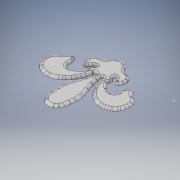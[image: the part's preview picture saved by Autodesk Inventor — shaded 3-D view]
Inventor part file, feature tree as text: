
AUTODESK INVENTOR PART (.ipt)
format: ipt  version: 2019 (Build 230136000, 136)  size: 981,504 bytes
history: native  units: mm
features: fillet x12, sketch x3, extrude x2
ambient origin geometry x8: Origin, YZ Plane, XZ Plane, XY Plane, X Axis, Y Axis, Z Axis, Center Point
bodies: Solid1 (feature_tree)
feature tree (17):
  extrude  "Extrusion1"  Depth=800.0mm
  fillet  "Fillet1"  Radius=300.0mm
  fillet  "Fillet2"  Radius=400.0mm
  fillet  "Fillet3"  Radius=200.0mm
  fillet  "Fillet4"  Radius=600.0mm
  fillet  "Fillet5"  Radius=1200.0mm
  fillet  "Fillet6"  Radius=2000.0mm
  fillet  "Fillet7"  Radius=100.0mm
  fillet  "Fillet8"  Radius=1200.0mm
  fillet  "Fillet9"  Radius=400.0mm
  fillet  "Fillet15"  Radius=300.0mm
  fillet  "Fillet16"  Radius=200.0mm
  fillet  "Fillet18"  Radius=1700.0mm
  sketch  "Sketch4"
  extrude  "Extrusion2"  [1 undecoded]
  sketch  "Sketch3"  dims[d0=2000.0mm d1=0.0mm d2=800.0mm d3=300.0mm d4=400.0mm d5=200.0mm d6=600.0mm d7=1200.0mm d8=2000.0mm d9=100.0mm d10=1200.0mm d16=400.0mm d17=300.0mm d19=200.0mm d20=1700.0mm d21=0.0mm]
  sketch  "Sketch5"
note: 1 required parameter value undecoded (feature->parameter linkage not recoverable at this tier; creation-order binding heuristic only, values carry confidence <= 0.55)
